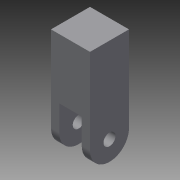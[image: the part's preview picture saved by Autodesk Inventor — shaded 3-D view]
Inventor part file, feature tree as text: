
AUTODESK INVENTOR PART (.ipt)
format: ipt  version: 2014 SP2 (Build 180246200, 246)  size: 112,128 bytes
history: native  units: mm
features: extrude x3, sketch x3, fillet x1
ambient origin geometry x8: Origin, YZ Plane, XZ Plane, XY Plane, X Axis, Y Axis, Z Axis, Center Point
bodies: Solid1 (feature_tree)
feature tree (7):
  extrude  "Extrusion1"  Depth=30.0mm
  extrude  "Extrusion2"  Depth=26.0mm
  fillet  "Fillet1"  Radius=26.0mm
  extrude  "Extrusion3"  Depth=40.0mm
  sketch  "Sketch1"  dims[d0=22.0mm d1=30.0mm]
  sketch  "Sketch2"  dims[d2=15.0mm d3=8.0mm d6=26.0mm d7=0.0mm]
  sketch  "Sketch3"  dims[d8=26.0mm d9=40.0mm d10=8.0mm d11=13.0mm d12=26.0mm d13=0.0mm d14=13.0mm d15=22.0mm d16=35.0mm d17=0.0mm]
